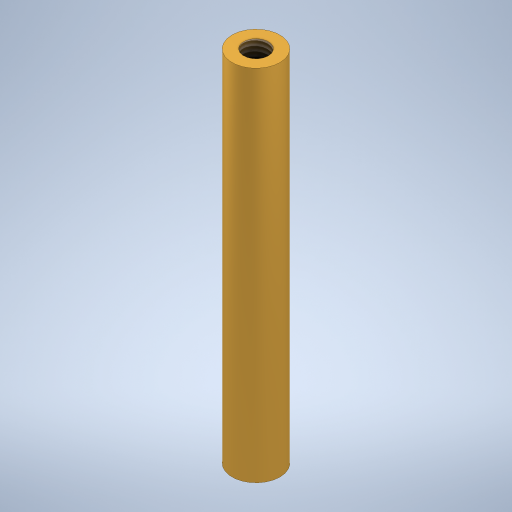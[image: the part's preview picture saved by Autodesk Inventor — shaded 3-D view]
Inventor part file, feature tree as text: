
AUTODESK INVENTOR PART (.ipt)
format: ipt  version: 2023.2 (Build 272271030, 271C)  size: 264,192 bytes
history: native  units: mm
features: hole x2, sketch x2, other x1, extrude x1
ambient origin geometry x8: Origin, YZ Plane, XZ Plane, XY Plane, X Axis, Y Axis, Z Axis, Center Point
bodies: Body1 (feature_tree)
feature tree (6):
  other  "Sólido1"
  extrude  "Extrusão1"  Depth=60.0mm TaperAngle=0.0deg
  hole  "Furo1"  [1 undecoded]
  hole  "Furo2"  [1 undecoded]
  sketch  "Esboço4"  dims[d1=8.0mm d2=60.0mm d3=0.0mm]
  sketch  "Esboço5"  dims[d14=4.134mm d15=10.0mm d16=3.023mm d17=2.0mm d18=14.3117mm d19=14.2mm d20=20.594885mm d21=4.134mm d22=10.0mm d23=4.0mm d24=2.0mm d25=90.0deg d26=14.2mm d27=20.594885mm d10=0.5mm d11=0.872665mm d12=0.5mm d13=0.872665mm]
note: 2 required parameter values undecoded (feature->parameter linkage not recoverable at this tier; creation-order binding heuristic only, values carry confidence <= 0.55)
